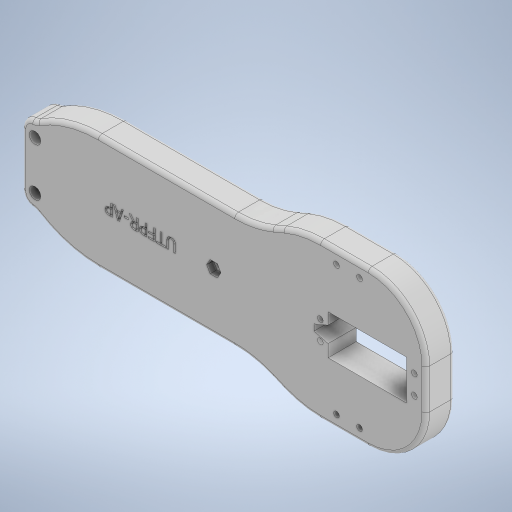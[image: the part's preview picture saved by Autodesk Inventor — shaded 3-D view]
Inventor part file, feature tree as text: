
AUTODESK INVENTOR PART (.ipt)
format: ipt  version: 2024.1 (Build 281209000, 209)  size: 681,472 bytes
history: native  units: mm
features: extrude x19, sketch x19, fillet x9, other x1
ambient origin geometry x8: Origin, YZ Plane, XZ Plane, XY Plane, X Axis, Y Axis, Z Axis, Center Point
bodies: Body1 (feature_tree)
feature tree (48):
  other  "Sólido1"
  extrude  "Extrusão1"  Depth=2.0mm
  extrude  "Extrusão2"  Depth=10.0mm
  extrude  "Extrusão3"  Depth=30.0mm
  extrude  "Extrusão4"  Depth=110.0mm
  extrude  "Extrusão5"  Depth=55.0mm
  fillet  "Arredondamento3"  Radius=110.0mm
  extrude  "Extrusão6"  Depth=15.0mm
  extrude  "Extrusão7"  Depth=30.0mm TaperAngle=0.0deg
  extrude  "Extrusão8"  Depth=10.0mm
  fillet  "Arredondamento5"  Radius=4.0mm
  fillet  "Arredondamento6"  Radius=30.0mm
  fillet  "Arredondamento7"  Radius=2.0mm
  fillet  "Arredondamento8"  Radius=10.0mm
  extrude  "Extrusão9"  Depth=4.0mm TaperAngle=0.0deg
  extrude  "Extrusão10"  Depth=2.0mm
  extrude  "Extrusão11"  Depth=20.0mm
  extrude  "Extrusão12"  Depth=20.0mm
  extrude  "Extrusão13"  Depth=10.0mm
  fillet  "Arredondamento11"  Radius=10.0mm
  extrude  "Extrusão14"  Depth=2.5mm
  fillet  "Arredondamento12"  Radius=5.0mm
  extrude  "Extrusão15"  Depth=10.0mm
  extrude  "Extrusão16"  Depth=15.0mm TaperAngle=0.0deg
  extrude  "Extrusão17"  Depth=15.0mm
  extrude  "Extrusão18"  Depth=30.0mm
  fillet  "Arredondamento13"  Radius=50.0mm
  extrude  "Extrusão19"  Depth=0.5mm
  fillet  "Arredondamento14"  Radius=3.0mm
  sketch  "Esboço1"  dims[d0=2.0mm d1=30.0mm]
  sketch  "Esboço2"  dims[d2=30.0mm d3=10.0mm]
  sketch  "Esboço3"  dims[d4=40.0mm d5=30.0mm]
  sketch  "Esboço4"  dims[d6=60.0mm d7=110.0mm]
  sketch  "Esboço5"  dims[d8=55.0mm d9=55.0mm d10=110.0mm]
  sketch  "Esboço8"  dims[d11=15.0mm d12=0.0mm d13=20.0mm]
  sketch  "Esboço9"  dims[d14=11.5mm d15=0.0mm d16=30.0mm d17=0.0mm]
  sketch  "Esboço10"  dims[d20=2.0mm d21=10.0mm d22=4.0mm d23=30.0mm d24=0.0mm d25=2.0mm d26=10.0mm]
  sketch  "Esboço11"  dims[d27=4.0mm d28=30.0mm d29=0.0mm]
  sketch  "Esboço13"  dims[d30=2.0mm d36=80.0mm]
  sketch  "Esboço14"  dims[d37=20.0mm d38=20.0mm]
  sketch  "Esboço15"  dims[d39=40.0mm d40=20.0mm]
  sketch  "Esboço16"  dims[d41=15.0mm d42=0.0mm d43=5.0mm d44=10.0mm]
  sketch  "Esboço17"  dims[d45=2.5mm d46=2.5mm d47=5.0mm]
  sketch  "Esboço18"  dims[d48=10.0mm d49=2.5mm]
  sketch  "Esboço19"  dims[d50=2.5mm d51=15.0mm d52=0.0mm]
  sketch  "Esboço20"  dims[d53=15.0mm d54=0.0mm d56=6.0mm]
  sketch  "Esboço21"  dims[d57=60.0mm d58=30.0mm d59=50.0mm]
  sketch  "Esboço22"  dims[d60=2.0mm d61=0.0mm d62=12.0mm d63=3.0mm d64=12.0mm d65=3.0mm d66=20.0mm d67=0.0mm d68=3.0mm d69=3.0mm d70=3.0mm d71=3.0mm d72=20.0mm d73=0.0mm d76=15.0mm d77=10.0mm d78=0.0mm d79=2.0mm d80=0.0mm d81=18.0mm d82=9.5mm d83=5.0mm d84=0.0mm d85=1.0mm d86=4.0mm d87=50.0mm d88=0.0mm d89=3.5mm d90=7.0mm d91=3.5mm d92=7.0mm d94=3.5mm d95=3.5mm d96=3.5mm d97=3.5mm d98=0.2mm d99=0.2mm d100=0.2mm d101=3.5mm d102=0.0mm d103=3.5mm d104=0.0mm d105=6.0mm d106=7.8mm d107=10.0mm d108=0.0mm d109=2.0mm d110=30.0mm d111=0.0mm d112=0.5mm]
